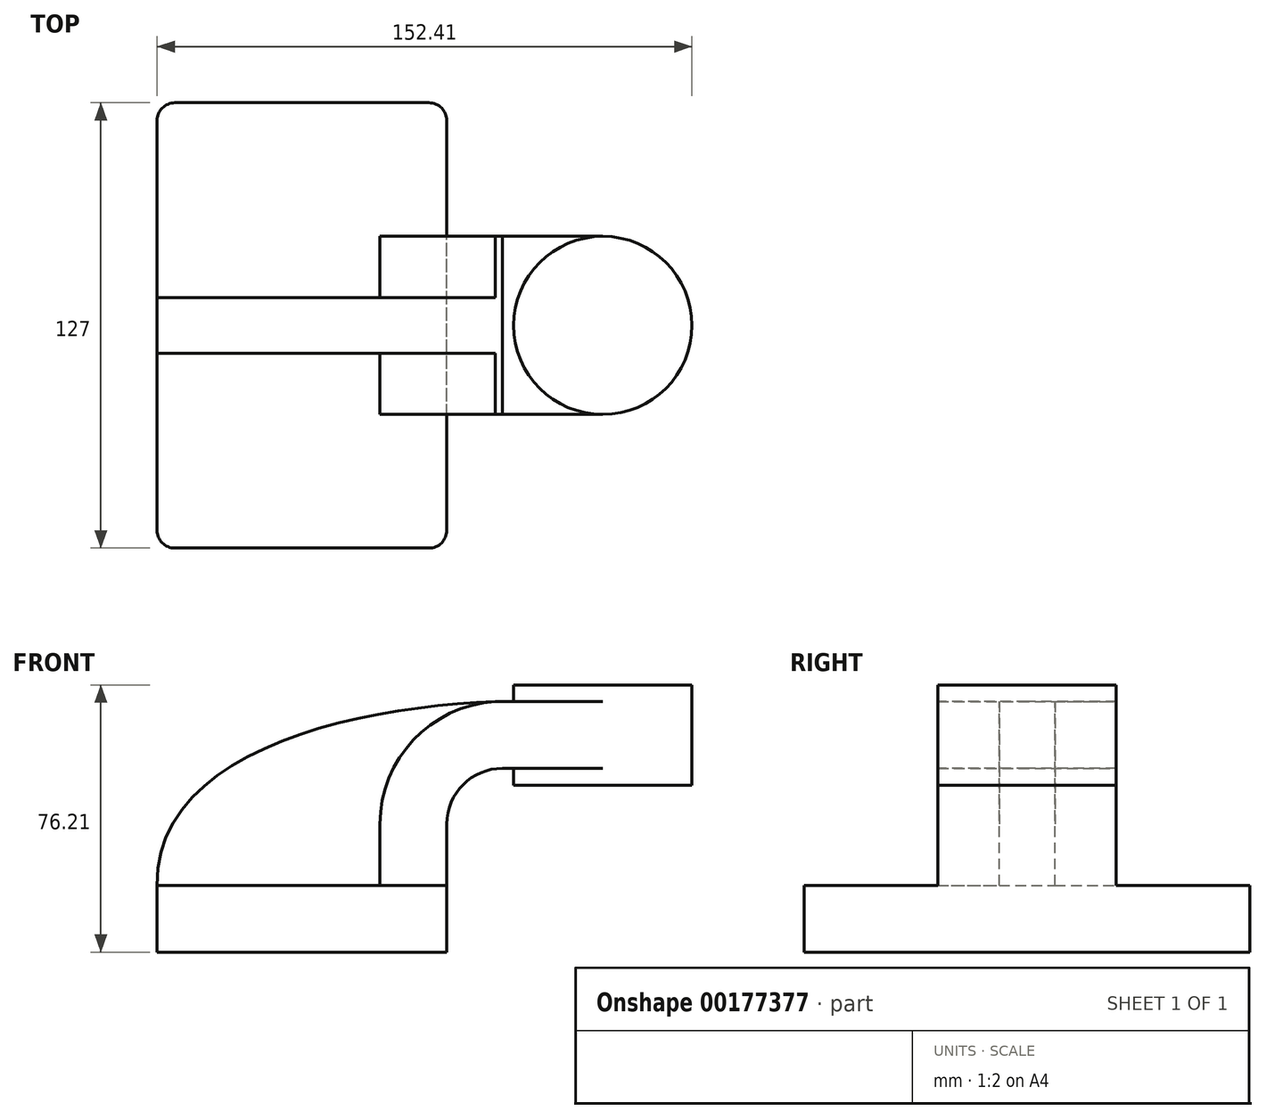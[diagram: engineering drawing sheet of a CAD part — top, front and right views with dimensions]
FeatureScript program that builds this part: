
annotation { "Feature Type Name" : "Feature", "Feature Type Description" : "" }
export const myFeature = defineFeature(function(context is Context, id is Id, definition is map)
    precondition{}
    {
        {
            var Q0;
            Q0=qCreatedBy(makeId("Front.planeOp"),FACE);
            var sketch = newSketch(context, id + "F0", { "sketchPlane" : qUnion([Q0])});
            skLineSegment(sketch, "E0.bottom", {"start": v(41.27, 9.53) * mm, "end": v(-41.28, 9.53) * mm});
            skLineSegment(sketch, "E0.top", {"start": v(41.28, -9.52) * mm, "end": v(-41.27, -9.52) * mm});
            skLineSegment(sketch, "E0.left", {"start": v(41.28, 9.53) * mm, "end": v(41.28, -9.52) * mm});
            skLineSegment(sketch, "E0.right", {"start": v(-41.28, 9.53) * mm, "end": v(-41.27, -9.52) * mm});
            skPoint(sketch, "E0.middle", {"position": v(0, 0) * mm});
            skLineSegment(sketch, "E1.bottom", {"start": v(111.12, 38.1) * mm, "end": v(60.32, 38.1) * mm});
            skLineSegment(sketch, "E1.top", {"start": v(111.12, 66.68) * mm, "end": v(60.32, 66.68) * mm});
            skLineSegment(sketch, "E1.left", {"start": v(111.12, 38.1) * mm, "end": v(111.12, 66.68) * mm});
            skLineSegment(sketch, "E1.right", {"start": v(60.32, 38.1) * mm, "end": v(60.32, 66.68) * mm});
            skPoint(sketch, "E1.middle", {"position": v(85.72, 52.39) * mm});
            skLineSegment(sketch, "E2", {"start": v(41.27, 9.53) * mm, "end": v(41.27, 27) * mm});
            skArc(sketch, "E3", {"start": v(41.27, 27) * mm, "mid": v(45.92, 38.23) * mm, "end": v(57.15, 42.88) * mm});
            skLineSegment(sketch, "E4", {"start": v(57.15, 42.88) * mm, "end": v(85.72, 42.88) * mm});
            skLineSegment(sketch, "E5.0", {"start": v(57.15, 61.93) * mm, "end": v(85.72, 61.93) * mm});
            skArc(sketch, "E5.1", {"start": v(22.23, 27) * mm, "mid": v(32.45, 51.7) * mm, "end": v(57.15, 61.93) * mm});
            skLineSegment(sketch, "E5.2", {"start": v(22.23, 9.53) * mm, "end": v(22.23, 27) * mm});
            skFitSpline(sketch, "E6", {"points": [v(-41.27, 9.53) * mm, v(57.15, 61.93) * mm], "startDerivative": vector(-1.7, 117.3) * mm, "endDerivative": vector(120.22, 2.97) * mm});
            skLineSegment(sketch, "E7", {"start": v(85.72, 61.93) * mm, "end": v(85.72, 42.88) * mm});
            skLineSegment(sketch, "E8", {"start": v(85.72, 38.1) * mm, "end": v(85.72, 66.68) * mm});
            skSolve(sketch);
        }
        {
            var Q0;
            Q0=makeQuery(id+"F0.imprint","IMPRINT",FACE,{"disambiguationData":[TD([[makeQuery(id+"F0.imprint","IMPRINT",EDGE,{"derivedFrom":sQuery(id+"F0.wireOp",EDGE,"E0.top")}),-1.0]])]});
            extrude(context, id + "F1", {"entities" : qUnion([Q0]), "endBound" : BoundingType.SYMMETRIC, "depth" : 127 * mm});
        }
        {
            var Q0;
            {var subQ1=sQuery(id+"F0.wireOp",EDGE,"E2");Q0=makeQuery(id+"F0.imprint","IMPRINT",FACE,{"disambiguationData":[TD([[makeQuery(id+"F0.imprint","IMPRINT",EDGE,{"derivedFrom":subQ1}),1.0]])]});}
            var Q1;
            {var subQ5=sQuery(id+"F0.wireOp",EDGE,"E7");Q1=makeQuery(id+"F0.imprint","IMPRINT",FACE,{"disambiguationData":[TD([[makeQuery(id+"F0.imprint","IMPRINT",EDGE,{"derivedFrom":subQ5}),-1.0]])]});}
            var Q2;
            {var subQ0=sQuery(id+"F0.wireOp",EDGE,"E4");var subQ1=sQuery(id+"F0.wireOp",EDGE,"E1.right");var subQ2=makeQuery(id+"F0.imprint","INTERSECT",VERTEX,{"derivedFrom":[subQ1,subQ0]});Q2=makeQuery(id+"F0.imprint","IMPRINT",FACE,{"disambiguationData":[TD([[makeQuery(id+"F0.imprint","IMPRINT",EDGE,{"disambiguationData":[TD([[subQ2,-1.0]])],"derivedFrom":subQ1}),-1.0]])]});}
            extrude(context, id + "F2", {"entities" : qUnion([Q0, Q1, Q2]), "operationType" : NewBodyOperationType.ADD, "endBound" : BoundingType.SYMMETRIC, "depth" : 50.8 * mm});
        }
        {
            var Q0;
            {var subQ3=sQuery(id+"F0.wireOp",EDGE,"E5.2");Q0=makeQuery(id+"F0.imprint","IMPRINT",FACE,{"disambiguationData":[TD([[makeQuery(id+"F0.imprint","IMPRINT",EDGE,{"derivedFrom":subQ3}),1.0]])]});}
            extrude(context, id + "F3", {"entities" : qUnion([Q0]), "operationType" : NewBodyOperationType.ADD, "endBound" : BoundingType.SYMMETRIC, "depth" : 15.88 * mm});
        }
        {
            var Q0;
            {var subQ4=sQuery(id+"F0.wireOp",EDGE,"E1.left");Q0=makeQuery(id+"F0.imprint","IMPRINT",FACE,{"disambiguationData":[TD([[makeQuery(id+"F0.imprint","IMPRINT",EDGE,{"derivedFrom":subQ4}),1.0]])]});}
            var Q1;
            Q1=sQuery(id+"F0.wireOp",EDGE,"E8");
            revolve(context, id + "F4", {"operationType" : NewBodyOperationType.ADD, "entities" : qUnion([Q0]), "axis" : qUnion([Q1]), "revolveType" : RevolveType.FULL});
        }
        {
            var Q0;
            Q0=makeQuery(id+"F1.opExtrude","CAP_EDGE",EDGE,{"disambiguationData":[OSD([sQuery(id+"F0.wireOp",EDGE,"E0.left")])],"isStart":false});
            var Q1;
            Q1=makeQuery(id+"F1.opExtrude","CAP_EDGE",EDGE,{"disambiguationData":[OSD([sQuery(id+"F0.wireOp",EDGE,"E0.right")])],"isStart":false});
            var Q2;
            Q2=makeQuery(id+"F1.opExtrude","CAP_EDGE",EDGE,{"disambiguationData":[OSD([sQuery(id+"F0.wireOp",EDGE,"E0.right")])],"isStart":true});
            var Q3;
            Q3=makeQuery(id+"F1.opExtrude","CAP_EDGE",EDGE,{"disambiguationData":[OSD([sQuery(id+"F0.wireOp",EDGE,"E0.left")])],"isStart":true});
            fillet(context, id + "F5", {"entities" : qUnion([Q0, Q1, Q2, Q3]), "radius" : 5.08 * mm, "tangentPropagation" : true, "allowEdgeOverflow" : false});
        }
    });
